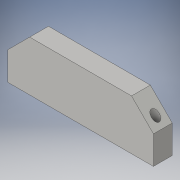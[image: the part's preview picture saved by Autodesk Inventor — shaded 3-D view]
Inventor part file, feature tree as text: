
AUTODESK INVENTOR PART (.ipt)
format: ipt  version: 2016 (Build 200138000, 138)  size: 113,152 bytes
history: native  units: in
note: dims shown in document units (in); Inventor stores cm internally (conversion verified against a paired STEP export)
features: extrude x1, chamfer x1, sketch x1
ambient origin geometry x8: Origin, YZ Plane, XZ Plane, XY Plane, X Axis, Y Axis, Z Axis, Center Point
bodies: Solid1 (feature_tree)
feature tree (3):
  extrude  "Extrusion1"  Depth=3.3244in
  chamfer  "Chamfer1"  Distance=0.429in
  sketch  "Sketch1"  dims[d0=3.3244in d1=0.429in d3=0.084in d4=0.084in d5=0.274in d6=3.3244in d7=0.429in d9=0.084in d10=0.084in d14=0.429in d15=0.1268in d16=0.1268in d17=0.084in d18=0.084in d19=0.1268in d20=0.1268in d21=2.981in d22=2.981in d23=3.3244in d24=1.143in d25=0.0in d26=0.5in d27=0.125in d28=45.0deg]
